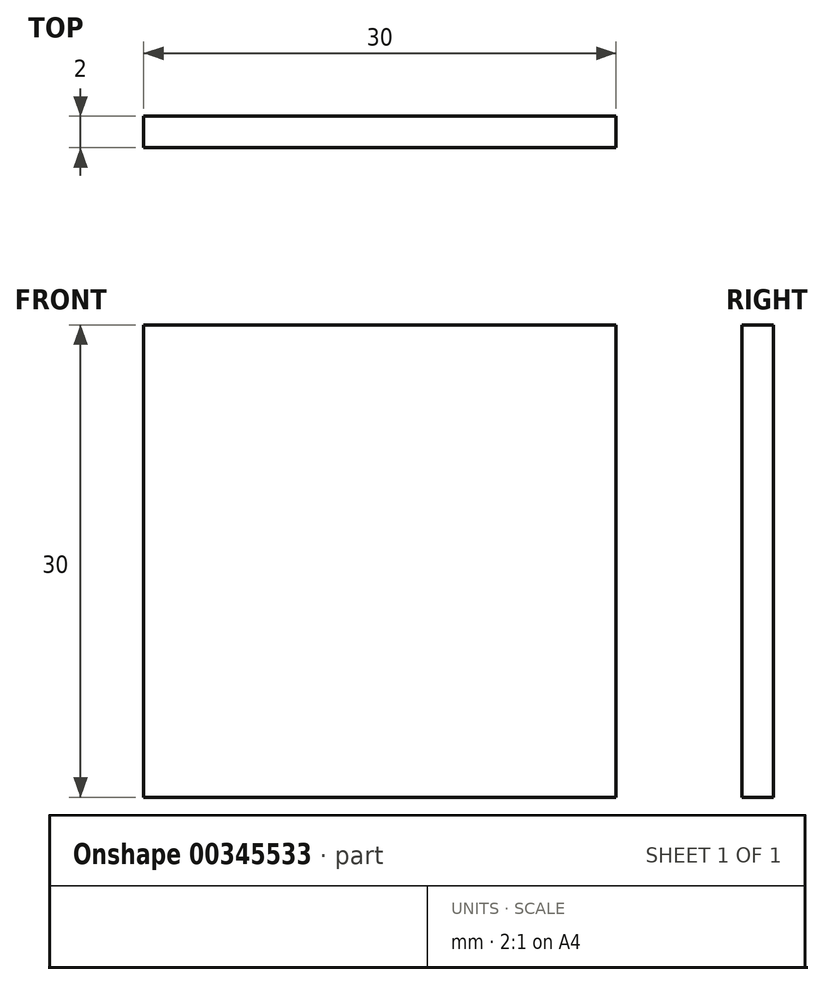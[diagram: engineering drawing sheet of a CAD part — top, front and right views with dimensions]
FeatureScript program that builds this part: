
annotation { "Feature Type Name" : "Feature", "Feature Type Description" : "" }
export const myFeature = defineFeature(function(context is Context, id is Id, definition is map)
    precondition{}
    {
        {
            var Q0;
            Q0=qCreatedBy(makeId("Top.planeOp"),FACE);
            var sketch = newSketch(context, id + "F0", { "sketchPlane" : qUnion([Q0])});
            skLineSegment(sketch, "E0.bottom", {"start": v(15, 1) * mm, "end": v(-15, 1) * mm});
            skLineSegment(sketch, "E0.top", {"start": v(15, -1) * mm, "end": v(-15, -1) * mm});
            skLineSegment(sketch, "E0.left", {"start": v(15, 1) * mm, "end": v(15, -1) * mm});
            skLineSegment(sketch, "E0.right", {"start": v(-15, 1) * mm, "end": v(-15, -1) * mm});
            skPoint(sketch, "E0.middle", {"position": v(0, 0) * mm});
            skSolve(sketch);
        }
        {
            var Q0;
            Q0 = qSketchRegion(id + "F0", true);
            extrude(context, id + "F1", {"entities" : qUnion([Q0]), "depth" : 30 * mm});
        }
    });
